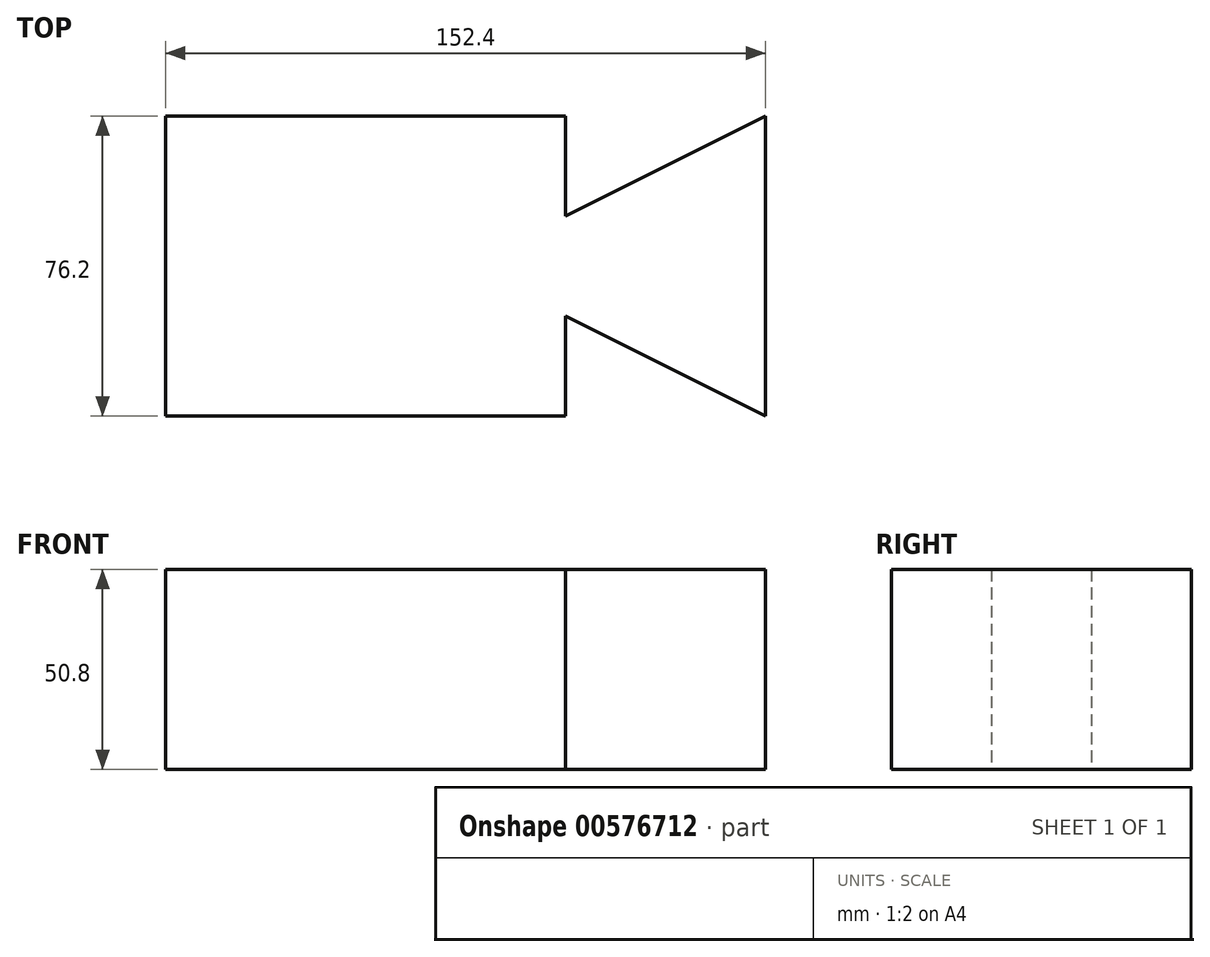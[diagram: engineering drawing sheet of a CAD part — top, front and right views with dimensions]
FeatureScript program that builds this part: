
annotation { "Feature Type Name" : "Feature", "Feature Type Description" : "" }
export const myFeature = defineFeature(function(context is Context, id is Id, definition is map)
    precondition{}
    {
        {
            var Q0;
            Q0=qCreatedBy(makeId("Top.planeOp"),FACE);
            var sketch = newSketch(context, id + "F0", { "sketchPlane" : qUnion([Q0])});
            skLineSegment(sketch, "E0", {"start": v(-70.23, 18.7) * mm, "end": v(-70.23, -57.5) * mm});
            skLineSegment(sketch, "E1", {"start": v(-70.23, -57.5) * mm, "end": v(31.37, -57.5) * mm});
            skLineSegment(sketch, "E2", {"start": v(31.37, -57.5) * mm, "end": v(31.37, 18.7) * mm});
            skLineSegment(sketch, "E3", {"start": v(31.37, 18.7) * mm, "end": v(-70.23, 18.7) * mm});
            skLineSegment(sketch, "E4", {"start": v(82.17, 18.7) * mm, "end": v(31.37, -6.7) * mm});
            skLineSegment(sketch, "E5", {"start": v(31.37, -32.1) * mm, "end": v(82.17, -57.5) * mm});
            skLineSegment(sketch, "E6", {"start": v(82.17, 18.7) * mm, "end": v(82.17, -57.5) * mm});
            skSolve(sketch);
        }
        {
            var Q0;
            {var subQ0=sQuery(id+"F0.wireOp",EDGE,"E4");Q0=makeQuery(id+"F0.imprint","IMPRINT",FACE,{"disambiguationData":[TD([[makeQuery(id+"F0.imprint","IMPRINT",EDGE,{"derivedFrom":subQ0}),1.0]])]});}
            extrude(context, id + "F1", {"entities" : qUnion([Q0]), "depth" : 25.4 * mm, "offsetDistance" : 25.4 * mm});
        }
        {
            var Q0;
            Q0 = qSketchRegion(id + "F0", true);
            extrude(context, id + "F2", {"entities" : qUnion([Q0]), "operationType" : NewBodyOperationType.ADD, "depth" : 50.8 * mm, "offsetDistance" : 25.4 * mm});
        }
    });
